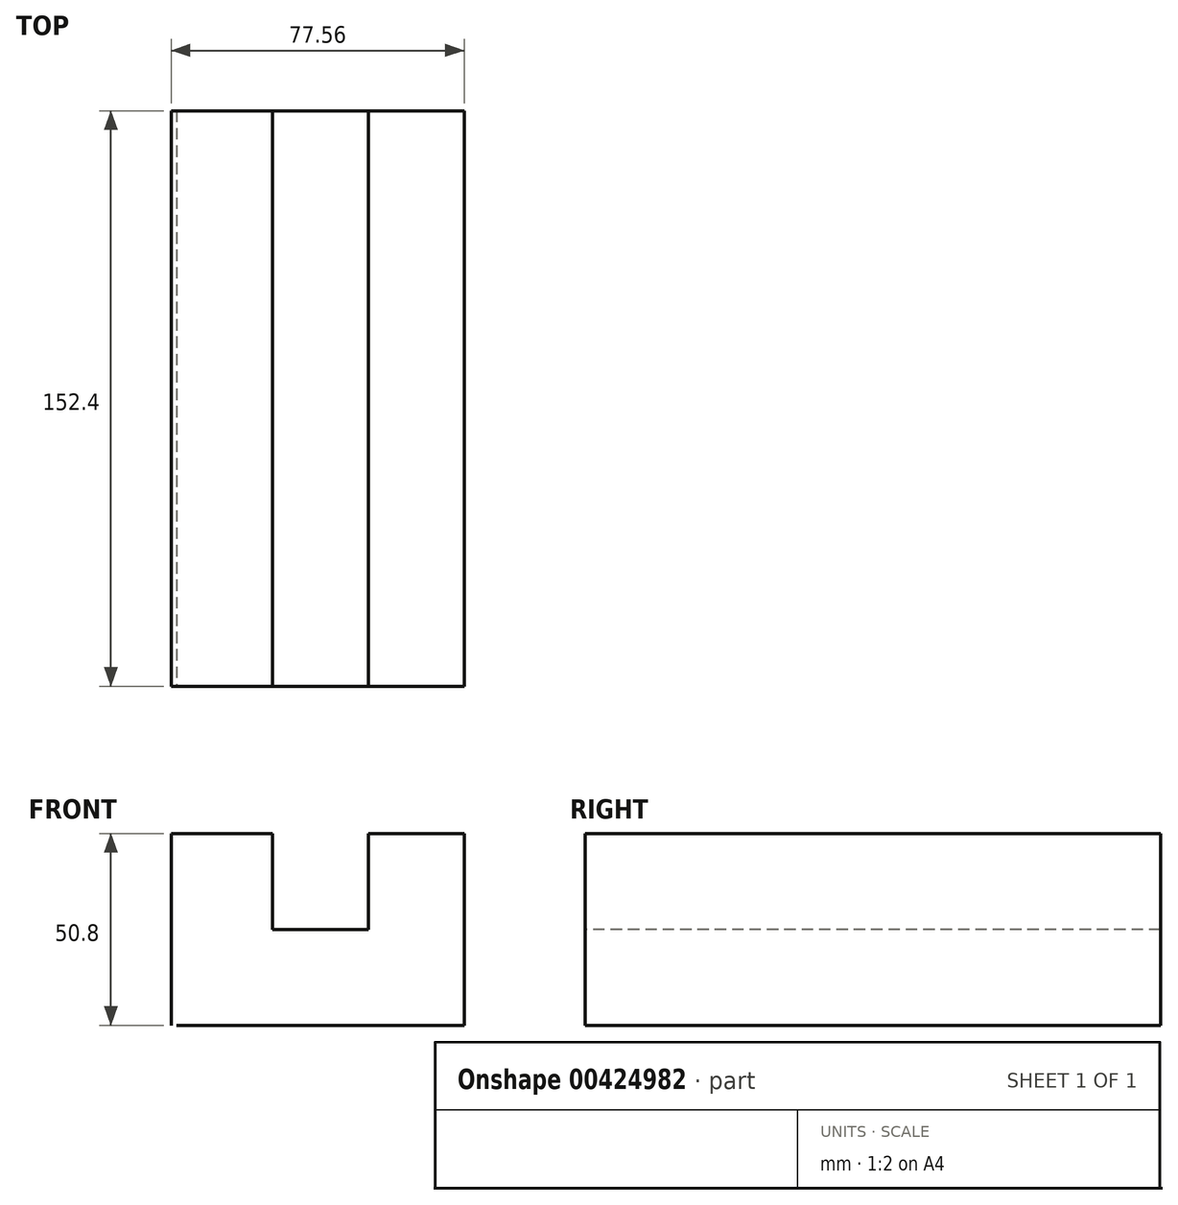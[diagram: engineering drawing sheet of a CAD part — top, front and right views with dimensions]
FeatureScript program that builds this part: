
annotation { "Feature Type Name" : "Feature", "Feature Type Description" : "" }
export const myFeature = defineFeature(function(context is Context, id is Id, definition is map)
    precondition{}
    {
        {
            var Q0;
            Q0=qCreatedBy(makeId("Front.planeOp"),FACE);
            var sketch = newSketch(context, id + "F0", { "sketchPlane" : qUnion([Q0])});
            skLineSegment(sketch, "E0", {"start": v(1.36, 0) * mm, "end": v(77.56, 0) * mm});
            skLineSegment(sketch, "E1", {"start": v(77.56, 0) * mm, "end": v(77.56, 50.8) * mm});
            skLineSegment(sketch, "E2", {"start": v(77.56, 50.8) * mm, "end": v(52.16, 50.8) * mm});
            skLineSegment(sketch, "E3", {"start": v(52.16, 50.8) * mm, "end": v(52.16, 25.4) * mm});
            skLineSegment(sketch, "E4", {"start": v(52.16, 25.4) * mm, "end": v(26.76, 25.4) * mm});
            skLineSegment(sketch, "E5", {"start": v(26.76, 25.4) * mm, "end": v(26.76, 50.8) * mm});
            skLineSegment(sketch, "E6", {"start": v(26.76, 50.8) * mm, "end": v(0, 50.8) * mm});
            skLineSegment(sketch, "E7", {"start": v(0, 50.8) * mm, "end": v(0, 0) * mm});
            skSolve(sketch);
        }
        {
            var Q0;
            Q0=sQuery(id+"F0.wireOp",EDGE,"E7");
            var Q1;
            Q1=sQuery(id+"F0.wireOp",EDGE,"E2");
            var Q2;
            Q2=sQuery(id+"F0.wireOp",EDGE,"E6");
            var Q3;
            Q3=sQuery(id+"F0.wireOp",EDGE,"E3");
            var Q4;
            Q4=sQuery(id+"F0.wireOp",EDGE,"E5");
            var Q5;
            Q5=sQuery(id+"F0.wireOp",EDGE,"E4");
            var Q6;
            Q6=sQuery(id+"F0.wireOp",EDGE,"E1");
            var Q7;
            Q7=sQuery(id+"F0.wireOp",EDGE,"E0");
            extrude(context, id + "F1", {"bodyType" : ToolBodyType.SURFACE, "operationType" : NewBodyOperationType.ADD, "surfaceEntities" : qUnion([Q0, Q1, Q2, Q3, Q4, Q5, Q6, Q7]), "depth" : 152.4 * mm});
        }
    });
